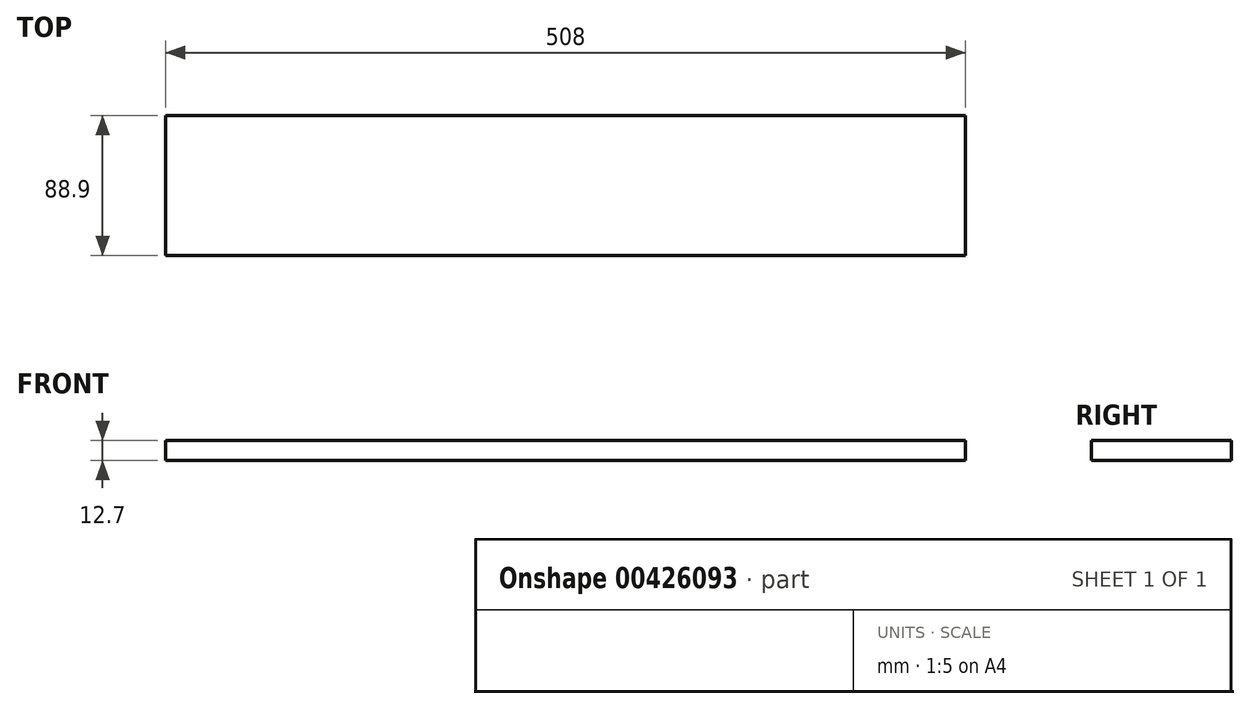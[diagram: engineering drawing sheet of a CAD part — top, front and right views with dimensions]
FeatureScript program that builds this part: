
annotation { "Feature Type Name" : "Feature", "Feature Type Description" : "" }
export const myFeature = defineFeature(function(context is Context, id is Id, definition is map)
    precondition{}
    {
        {
            var Q0;
            Q0=qCreatedBy(makeId("Top.planeOp"),FACE);
            var sketch = newSketch(context, id + "F0", { "sketchPlane" : qUnion([Q0])});
            skLineSegment(sketch, "E0.bottom", {"start": v(254, -44.45) * mm, "end": v(-254, -44.45) * mm});
            skLineSegment(sketch, "E0.top", {"start": v(254, 44.45) * mm, "end": v(-254, 44.45) * mm});
            skLineSegment(sketch, "E0.left", {"start": v(254, -44.45) * mm, "end": v(254, 44.45) * mm});
            skLineSegment(sketch, "E0.right", {"start": v(-254, -44.45) * mm, "end": v(-254, 44.45) * mm});
            skPoint(sketch, "E0.middle", {"position": v(0, 0) * mm});
            skSolve(sketch);
        }
        {
            var Q0;
            Q0=qSketchRegion(id+"F0",true);
            extrude(context, id + "F1", {"entities" : qUnion([Q0]), "depth" : 12.7 * mm});
        }
    });
